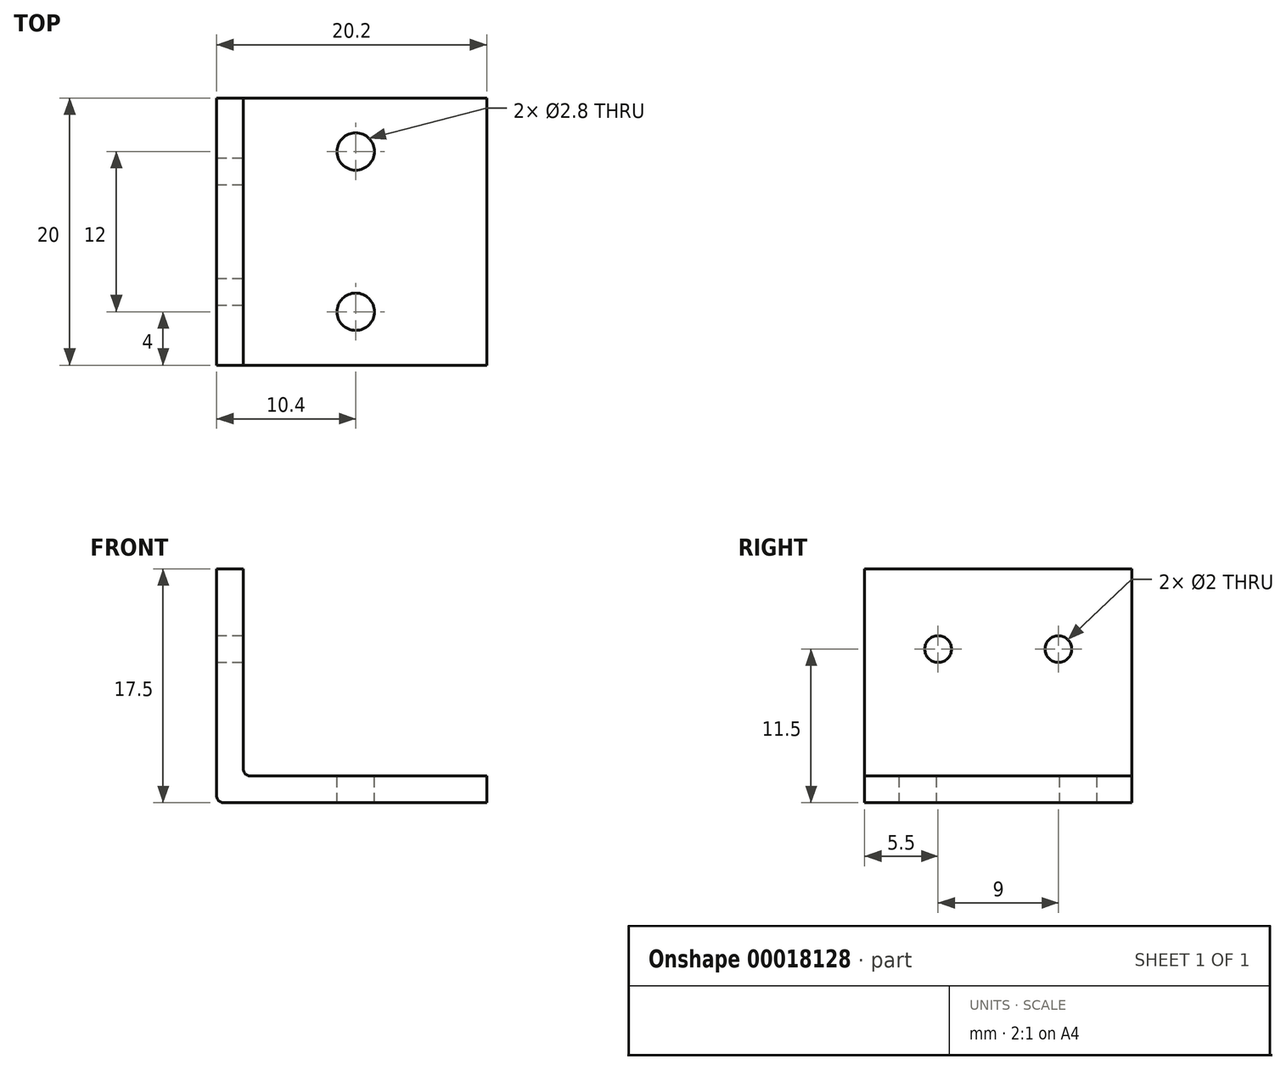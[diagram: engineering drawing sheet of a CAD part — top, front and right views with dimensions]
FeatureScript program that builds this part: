
annotation { "Feature Type Name" : "Feature", "Feature Type Description" : "" }
export const myFeature = defineFeature(function(context is Context, id is Id, definition is map)
    precondition{}
    {
        {
            var Q0;
            Q0=qCreatedBy(makeId("Front.planeOp"),FACE);
            var sketch = newSketch(context, id + "F0", { "sketchPlane" : qUnion([Q0])});
            skLineSegment(sketch, "E0", {"start": v(0, 0) * mm, "end": v(20.2, 0) * mm});
            skLineSegment(sketch, "E1", {"start": v(20.2, 0) * mm, "end": v(20.2, 2) * mm});
            skLineSegment(sketch, "E2", {"start": v(20.2, 2) * mm, "end": v(2, 2) * mm});
            skLineSegment(sketch, "E3", {"start": v(2, 2) * mm, "end": v(2, 17.5) * mm});
            skLineSegment(sketch, "E4", {"start": v(2, 17.5) * mm, "end": v(0, 17.5) * mm});
            skLineSegment(sketch, "E5", {"start": v(0, 17.5) * mm, "end": v(0, 0) * mm});
            skSolve(sketch);
        }
        {
            var Q0;
            Q0=makeQuery(id+"F0.imprint","IMPRINT",FACE,{"disambiguationData":[TD([[makeQuery(id+"F0.imprint","IMPRINT",EDGE,{"derivedFrom":sQuery(id+"F0.wireOp",EDGE,"E0")}),1.0]])]});
            extrude(context, id + "F1", {"entities" : qUnion([Q0]), "depth" : 20 * mm});
        }
        {
            var Q0;
            Q0=makeQuery(id+"F1.opExtrude","SWEPT_FACE",FACE,{"disambiguationData":[OSD([sQuery(id+"F0.wireOp",EDGE,"E2")])]});
            var sketch = newSketch(context, id + "F2", { "sketchPlane" : qUnion([Q0])});
            skCircle(sketch, "E6", {"center": v(10.4, -4) * mm, "radius": 1.4 * mm});
            skCircle(sketch, "E7", {"center": v(10.4, -16) * mm, "radius": 1.4 * mm});
            skSolve(sketch);
        }
        {
            var Q0;
            Q0=makeQuery(id+"F2.imprint","IMPRINT",FACE,{"disambiguationData":[TD([[makeQuery(id+"F2.imprint","IMPRINT",EDGE,{"derivedFrom":sQuery(id+"F2.wireOp",EDGE,"E6")}),1.0]])]});
            var Q1;
            Q1=makeQuery(id+"F2.imprint","IMPRINT",FACE,{"disambiguationData":[TD([[makeQuery(id+"F2.imprint","IMPRINT",EDGE,{"derivedFrom":sQuery(id+"F2.wireOp",EDGE,"E7")}),1.0]])]});
            extrude(context, id + "F3", {"entities" : qUnion([Q0, Q1]), "operationType" : NewBodyOperationType.REMOVE, "oppositeDirection" : true, "depth" : 25 * mm});
        }
        {
            var Q0;
            Q0=makeQuery(id+"F1.opExtrude","SWEPT_FACE",FACE,{"disambiguationData":[OSD([sQuery(id+"F0.wireOp",EDGE,"E3")])]});
            var sketch = newSketch(context, id + "F4", { "sketchPlane" : qUnion([Q0])});
            skCircle(sketch, "E8", {"center": v(-14.5, 11.5) * mm, "radius": 1 * mm});
            skCircle(sketch, "E9", {"center": v(-5.5, 11.5) * mm, "radius": 1 * mm});
            skSolve(sketch);
        }
        {
            var Q0;
            Q0=makeQuery(id+"F4.imprint","IMPRINT",FACE,{"disambiguationData":[TD([[makeQuery(id+"F4.imprint","IMPRINT",EDGE,{"derivedFrom":sQuery(id+"F4.wireOp",EDGE,"E8")}),1.0]])]});
            var Q1;
            Q1=makeQuery(id+"F4.imprint","IMPRINT",FACE,{"disambiguationData":[TD([[makeQuery(id+"F4.imprint","IMPRINT",EDGE,{"derivedFrom":sQuery(id+"F4.wireOp",EDGE,"E9")}),1.0]])]});
            extrude(context, id + "F5", {"entities" : qUnion([Q0, Q1]), "operationType" : NewBodyOperationType.REMOVE, "oppositeDirection" : true, "depth" : 25 * mm});
        }
        {
            var Q0;
            Q0=makeQuery(id+"F1.opExtrude","SWEPT_EDGE",EDGE,{"disambiguationData":[OSD([sQuery(id+"F0.wireOp",EDGE,"E2"),sQuery(id+"F0.wireOp",EDGE,"E3")])]});
            var Q1;
            Q1=makeQuery(id+"F1.opExtrude","SWEPT_EDGE",EDGE,{"disambiguationData":[OSD([sQuery(id+"F0.wireOp",EDGE,"E0"),sQuery(id+"F0.wireOp",EDGE,"E5")])]});
            fillet(context, id + "F6", {"entities" : qUnion([Q0, Q1]), "radius" : 0.5 * mm, "allowEdgeOverflow" : false});
        }
    });
